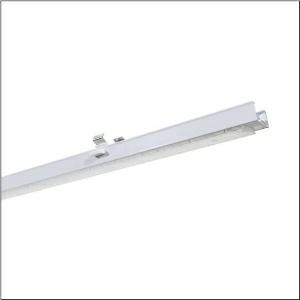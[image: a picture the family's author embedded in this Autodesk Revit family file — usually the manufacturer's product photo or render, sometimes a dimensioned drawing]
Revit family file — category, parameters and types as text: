
# Revit family: trunking_flex_31_51re18mb4cb
name_source: partatom
category: Lighting Fixtures
units: mm (PartAtom-declared; Revit-internal decimal feet)

## family parameters
Cut with Voids When Loaded = No
Host = Face
Light Source = No
Part Type = Normal
Room Calculation Point = No
Round Connector Dimension = Use Diameter
Shared = No

## types (1)
- --- (1 x LED, 11500 lm, 66 W, 4000K)
    Apparent Load = 66 VA
    CIE Flux Codes = 71 89 97 97 100
    Color Rendering = 80
    Color Temperature = 4000K
    Default Elevation = 1800 mm
    Description = Trunking Flex 31, luminaire insert, of extruded aluminium section, coated, traffic white (RAL 9016), length: 1.472mm, width: 91mm, height: 53mm, LED rated luminous flux: 11.500lm, light colour: 840, control gear: ON/OFF Multilumen, with system connector: socket, mains connection: 220..240V, AC, 50/60Hz, rated input power: 66W, connected load according to luminous flux setting (19/24/32/37/47/52/60/66W), luminous flux adjustable on luminaire in eight steps (3450/4380/5800/6700/8350/9200/10500/11500lm ), primary light control with lens, of plastic, primary optical cover: cover, of PMMA, light emission: direct distribution, protection rating (complete): IP20, insulation class (complete): insulation class I (protective earthing), certification: CE, UKCA, impact resistance: IK02, permissible ambient temperature for indoor applications: -20..+40°C, packaging unit: 1 piece
    Height = 58 mm
    Lamp = 1 x LED
    Lamp Light Flux = 11500 lm
    Lamp Power = 66 W
    Lamp count = 1
    Length = 1472 mm
    Luminous efficacy = 174 lm/W
    Manufacturer = Siteco
    ModVariant = No
    Model = 51RE18MB4CB
    Mounting Place = Ceiling
    Mounting Type = Pendant
    Number of Poles = 1
    OnlyDefault = Yes
    Power Factor = 1
    Product Name = Trunking Flex 31
    Product group = luminaire insert
    ProductGroupID = 902
    Protection Class = Protection class I
    Protection Degree = IP 20
    RLX_Detail_Level = 1
    RLX_Emergency_Light_Flux = 0 lm
    RLX_Emergency_Type = 0
    RLX_Emergency_Type_DB = No
    RlxData = <blob elided: 21149 chars, md5=ca15bdf6>
    Socket = socket
    Standby Power = 0 W
    System Light Flux = 11500 lm
    System Power = 66 W
    Type Comments = factory setting: luminous flux: 100 % | (ON | ON | ON)
    Type Image = l_1266702.jpg
    URL = http://relux.com
    VarID = @adj_059062
    Voltage = 0 V
    Weight = 0.00 kg
    Width = 65 mm

## geometry (parser evidence)
native form markers: Blend x4, Sweep x12
no freeform markers — native parametric forms only
